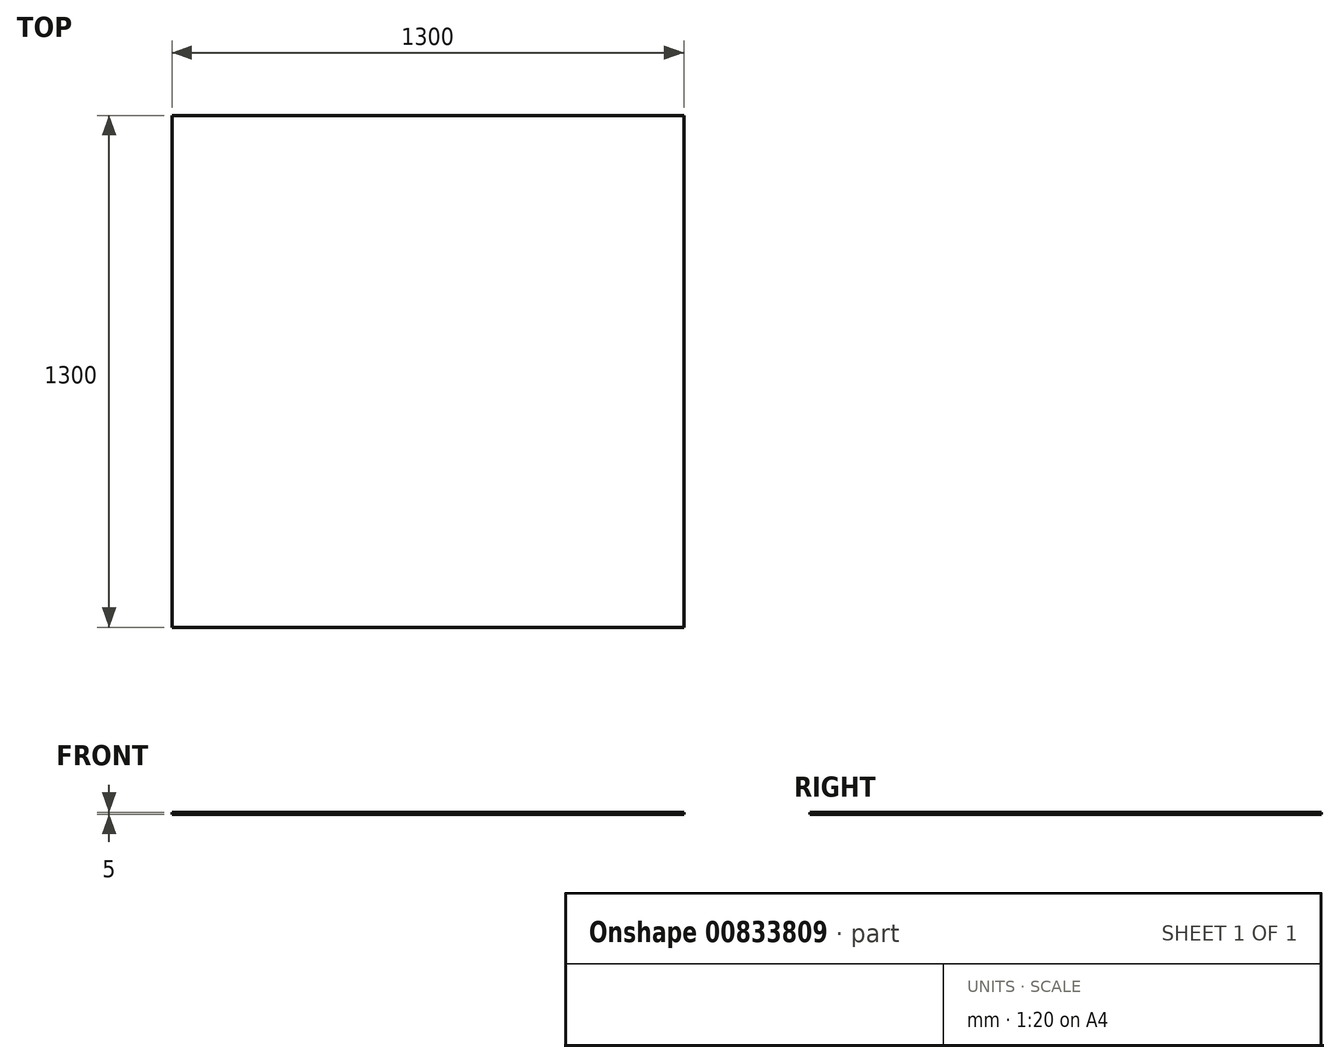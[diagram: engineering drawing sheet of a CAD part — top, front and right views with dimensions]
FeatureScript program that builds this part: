
annotation { "Feature Type Name" : "Feature", "Feature Type Description" : "" }
export const myFeature = defineFeature(function(context is Context, id is Id, definition is map)
    precondition{}
    {
        {
            var Q0;
            Q0=qCreatedBy(makeId("Top.planeOp"),FACE);
            var sketch = newSketch(context, id + "F0", { "sketchPlane" : qUnion([Q0])});
            skLineSegment(sketch, "E0", {"start": v(0, 0) * mm, "end": v(0, 1300) * mm});
            skLineSegment(sketch, "E1", {"start": v(0, 1300) * mm, "end": v(-1300, 1300) * mm});
            skLineSegment(sketch, "E2", {"start": v(-1300, 1300) * mm, "end": v(-1300, 0) * mm});
            skLineSegment(sketch, "E3", {"start": v(-1300, 0) * mm, "end": v(0, 0) * mm});
            skSolve(sketch);
        }
        {
            var Q0;
            Q0=makeQuery(id+"F0.imprint","IMPRINT",FACE,{"disambiguationData":[TD([[makeQuery(id+"F0.imprint","IMPRINT",EDGE,{"derivedFrom":sQuery(id+"F0.wireOp",EDGE,"E0")}),1.0]])]});
            extrude(context, id + "F1", {"entities" : qUnion([Q0]), "depth" : 5 * mm, "offsetDistance" : 25 * mm});
        }
    });
